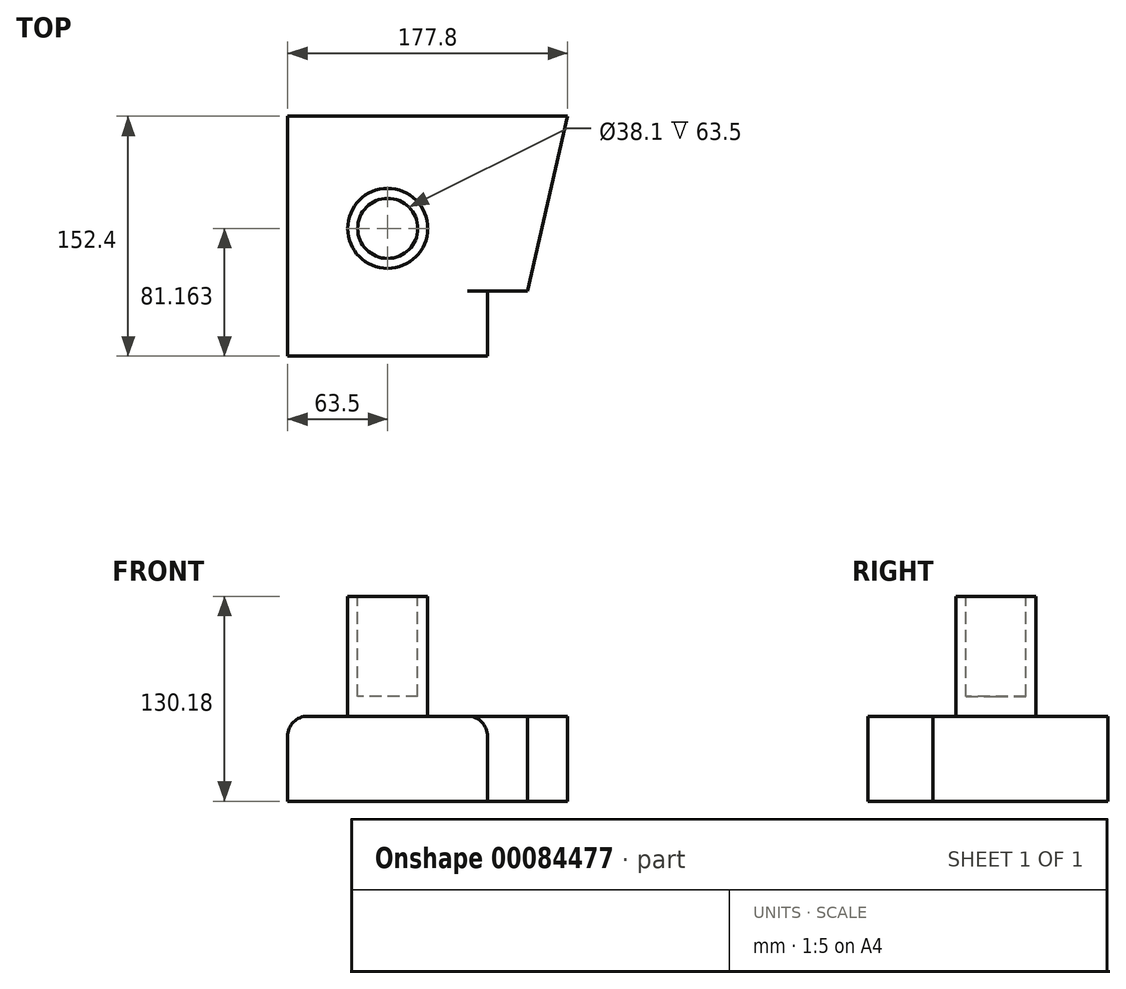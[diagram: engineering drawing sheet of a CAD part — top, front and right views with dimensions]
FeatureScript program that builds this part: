
annotation { "Feature Type Name" : "Feature", "Feature Type Description" : "" }
export const myFeature = defineFeature(function(context is Context, id is Id, definition is map)
    precondition{}
    {
        {
            var Q0;
            Q0=qCreatedBy(makeId("Top.planeOp"),FACE);
            var sketch = newSketch(context, id + "F0", { "sketchPlane" : qUnion([Q0])});
            skLineSegment(sketch, "E0.bottom", {"start": v(0, 0) * mm, "end": v(177.8, 0) * mm});
            skLineSegment(sketch, "E0.top", {"start": v(0, 152.4) * mm, "end": v(177.8, 152.4) * mm});
            skLineSegment(sketch, "E0.left", {"start": v(0, 0) * mm, "end": v(0, 152.4) * mm});
            skLineSegment(sketch, "E0.right", {"start": v(177.8, 0) * mm, "end": v(177.8, 152.4) * mm});
            skLineSegment(sketch, "E1", {"start": v(0, 0) * mm, "end": v(127, 0) * mm});
            skLineSegment(sketch, "E2", {"start": v(127, 0) * mm, "end": v(127, 41.28) * mm});
            skLineSegment(sketch, "E3", {"start": v(127, 41.28) * mm, "end": v(152.4, 41.28) * mm});
            skLineSegment(sketch, "E4", {"start": v(152.4, 41.27) * mm, "end": v(177.8, 152.4) * mm});
            skSolve(sketch);
        }
        {
            var Q0;
            Q0=makeQuery(id+"F0.imprint","IMPRINT",FACE,{"disambiguationData":[TD([[makeQuery(id+"F0.imprint","IMPRINT",EDGE,{"derivedFrom":sQuery(id+"F0.wireOp",EDGE,"E0.top")}),-1.0]])]});
            extrude(context, id + "F1", {"entities" : qUnion([Q0]), "depth" : 53.97 * mm});
        }
        {
            var Q0;
            Q0=makeQuery(id+"F1.opExtrude","CAP_FACE",FACE,{"disambiguationData":[OSD([sQuery(id+"F0.wireOp",EDGE,"E0.top"),sQuery(id+"F0.wireOp",EDGE,"E0.left"),sQuery(id+"F0.wireOp",EDGE,"E1"),sQuery(id+"F0.wireOp",EDGE,"E2"),sQuery(id+"F0.wireOp",EDGE,"E3"),sQuery(id+"F0.wireOp",EDGE,"E4")])],"isStart":false});
            var sketch = newSketch(context, id + "F2", { "sketchPlane" : qUnion([Q0])});
            skLineSegment(sketch, "E5.bottom", {"start": v(0, 152.4) * mm, "end": v(63.5, 152.4) * mm});
            skLineSegment(sketch, "E5.top", {"start": v(0, 81.16) * mm, "end": v(63.5, 81.16) * mm});
            skLineSegment(sketch, "E5.left", {"start": v(0, 152.4) * mm, "end": v(0, 81.16) * mm});
            skLineSegment(sketch, "E5.right", {"start": v(63.5, 152.4) * mm, "end": v(63.5, 81.16) * mm});
            skCircle(sketch, "E6", {"center": v(63.5, 81.16) * mm, "radius": 25.4 * mm});
            skCircle(sketch, "E7", {"center": v(63.5, 81.16) * mm, "radius": 19.05 * mm});
            skSolve(sketch);
        }
        {
            var Q0;
            {var subQ0=sQuery(id+"F2.wireOp",EDGE,"E6");var subQ1=sQuery(id+"F2.wireOp",EDGE,"E5.top");var subQ2=makeQuery(id+"F2.imprint","INTERSECT",VERTEX,{"derivedFrom":[subQ1,subQ0]});Q0=makeQuery(id+"F2.imprint","IMPRINT",FACE,{"disambiguationData":[TD([[makeQuery(id+"F2.imprint","IMPRINT",EDGE,{"disambiguationData":[TD([[subQ2,-1.0]])],"derivedFrom":subQ1}),1.0]])]});}
            var Q1;
            {var subQ0=sQuery(id+"F2.wireOp",EDGE,"E6");var subQ1=sQuery(id+"F2.wireOp",EDGE,"E5.top");var subQ2=makeQuery(id+"F2.imprint","INTERSECT",VERTEX,{"derivedFrom":[subQ1,subQ0]});Q1=makeQuery(id+"F2.imprint","IMPRINT",FACE,{"disambiguationData":[TD([[makeQuery(id+"F2.imprint","IMPRINT",EDGE,{"disambiguationData":[TD([[subQ2,-1.0]])],"derivedFrom":subQ1}),-1.0]])]});}
            var Q2;
            {var subQ0=sQuery(id+"F2.wireOp",EDGE,"E5.right");var subQ1=sQuery(id+"F2.wireOp",EDGE,"E5.top");var subQ2=makeQuery(id+"F2.imprint","INTERSECT",VERTEX,{"derivedFrom":[subQ1,subQ0]});Q2=makeQuery(id+"F2.imprint","IMPRINT",FACE,{"disambiguationData":[TD([[makeQuery(id+"F2.imprint","IMPRINT",EDGE,{"disambiguationData":[TD([[subQ2,1.0]])],"derivedFrom":subQ1}),-1.0]])]});}
            var Q3;
            {var subQ0=sQuery(id+"F2.wireOp",EDGE,"E5.right");var subQ1=sQuery(id+"F2.wireOp",EDGE,"E5.top");var subQ2=makeQuery(id+"F2.imprint","INTERSECT",VERTEX,{"derivedFrom":[subQ1,subQ0]});Q3=makeQuery(id+"F2.imprint","IMPRINT",FACE,{"disambiguationData":[TD([[makeQuery(id+"F2.imprint","IMPRINT",EDGE,{"disambiguationData":[TD([[subQ2,1.0]])],"derivedFrom":subQ1}),1.0]])]});}
            extrude(context, id + "F3", {"entities" : qUnion([Q0, Q1, Q2, Q3]), "operationType" : NewBodyOperationType.ADD, "depth" : 76.2 * mm});
        }
        {
            var Q0;
            Q0=makeQuery(id+"F3.opExtrude","CAP_FACE",FACE,{"disambiguationData":[OSD([sQuery(id+"F2.wireOp",EDGE,"E6")])],"isStart":false});
            var sketch = newSketch(context, id + "F4", { "sketchPlane" : qUnion([Q0])});
            skCircle(sketch, "E8", {"center": v(63.5, 81.16) * mm, "radius": 19.05 * mm});
            skSolve(sketch);
        }
        {
            var Q0;
            Q0=makeQuery(id+"F4.imprint","IMPRINT",FACE,{"disambiguationData":[TD([[makeQuery(id+"F4.imprint","IMPRINT",EDGE,{"derivedFrom":sQuery(id+"F4.wireOp",EDGE,"E8")}),1.0]])]});
            extrude(context, id + "F5", {"entities" : qUnion([Q0]), "operationType" : NewBodyOperationType.REMOVE, "oppositeDirection" : true, "depth" : 63.5 * mm});
        }
        {
            var Q0;
            Q0=makeQuery(id+"F3.opExtrude","CAP_EDGE",EDGE,{"disambiguationData":[OSD([sQuery(id+"F2.wireOp",EDGE,"E6")])],"isStart":true});
            var Q1;
            Q1=makeQuery(id+"F1.opExtrude","CAP_EDGE",EDGE,{"disambiguationData":[OSD([sQuery(id+"F0.wireOp",EDGE,"E2")])],"isStart":false});
            var Q2;
            Q2=makeQuery(id+"F1.opExtrude","CAP_EDGE",EDGE,{"disambiguationData":[OSD([sQuery(id+"F0.wireOp",EDGE,"E1")])],"isStart":false});
            fillet(context, id + "F6", {"entities" : qUnion([Q0, Q1, Q2]), "radius" : 12.7 * mm, "tangentPropagation" : true, "allowEdgeOverflow" : false});
        }
        {
            var Q0;
            Q0=makeQuery(id+"F1.opExtrude","CAP_EDGE",EDGE,{"disambiguationData":[OSD([sQuery(id+"F0.wireOp",EDGE,"E0.left")])],"isStart":false});
            fillet(context, id + "F7", {"entities" : qUnion([Q0]), "radius" : 12.7 * mm, "tangentPropagation" : true, "allowEdgeOverflow" : false});
        }
    });
